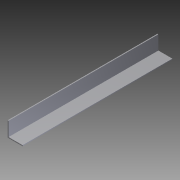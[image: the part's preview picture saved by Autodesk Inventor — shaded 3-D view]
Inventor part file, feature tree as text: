
AUTODESK INVENTOR PART (.ipt)
format: ipt  version: 2012 (Build 160160000, 160)  size: 73,216 bytes
history: native  units: in
note: dims shown in document units (in); Inventor stores cm internally (conversion verified against a paired STEP export)
features: extrude x1, sketch x1
ambient origin geometry x8: Origin, YZ Plane, XZ Plane, XY Plane, X Axis, Y Axis, Z Axis, Center Point
bodies: Solid1 (feature_tree)
feature tree (2):
  extrude  "Extrusion1"  Depth=0.9996in
  sketch  "Sketch1"  dims[d0=1.0in d1=0.9996in d2=0.0625in d3=0.0625in d4=10.0in d5=0.0in]
